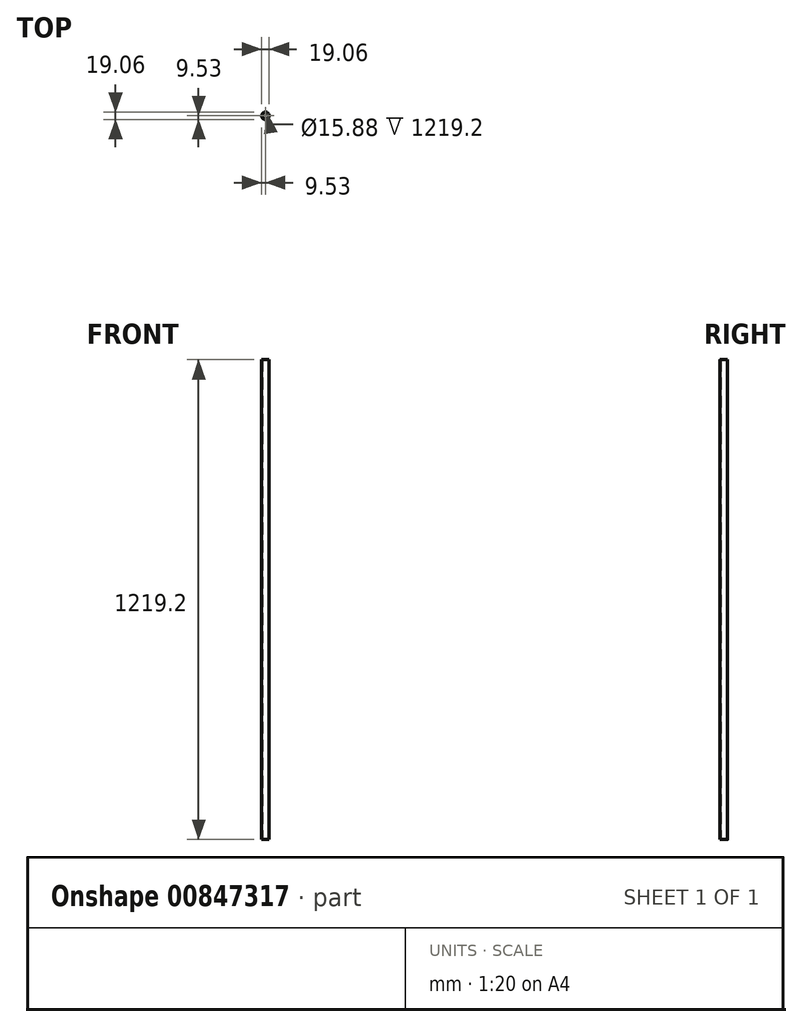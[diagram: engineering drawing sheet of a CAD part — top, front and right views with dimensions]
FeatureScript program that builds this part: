
annotation { "Feature Type Name" : "Feature", "Feature Type Description" : "" }
export const myFeature = defineFeature(function(context is Context, id is Id, definition is map)
    precondition{}
    {
        {
            var Q0;
            Q0=qCreatedBy(makeId("Top.planeOp"),FACE);
            var sketch = newSketch(context, id + "F0", { "sketchPlane" : qUnion([Q0])});
            skCircle(sketch, "E0", {"center": v(0, 0) * mm, "radius": 9.53 * mm});
            skCircle(sketch, "E1", {"center": v(0, 0) * mm, "radius": 7.94 * mm});
            skSolve(sketch);
        }
        {
            var Q0;
            Q0 = qSketchRegion(id + "F0", true);
            extrude(context, id + "F1", {"entities" : qUnion([Q0]), "depth" : 1219.2 * mm, "offsetDistance" : 25.4 * mm});
        }
    });
